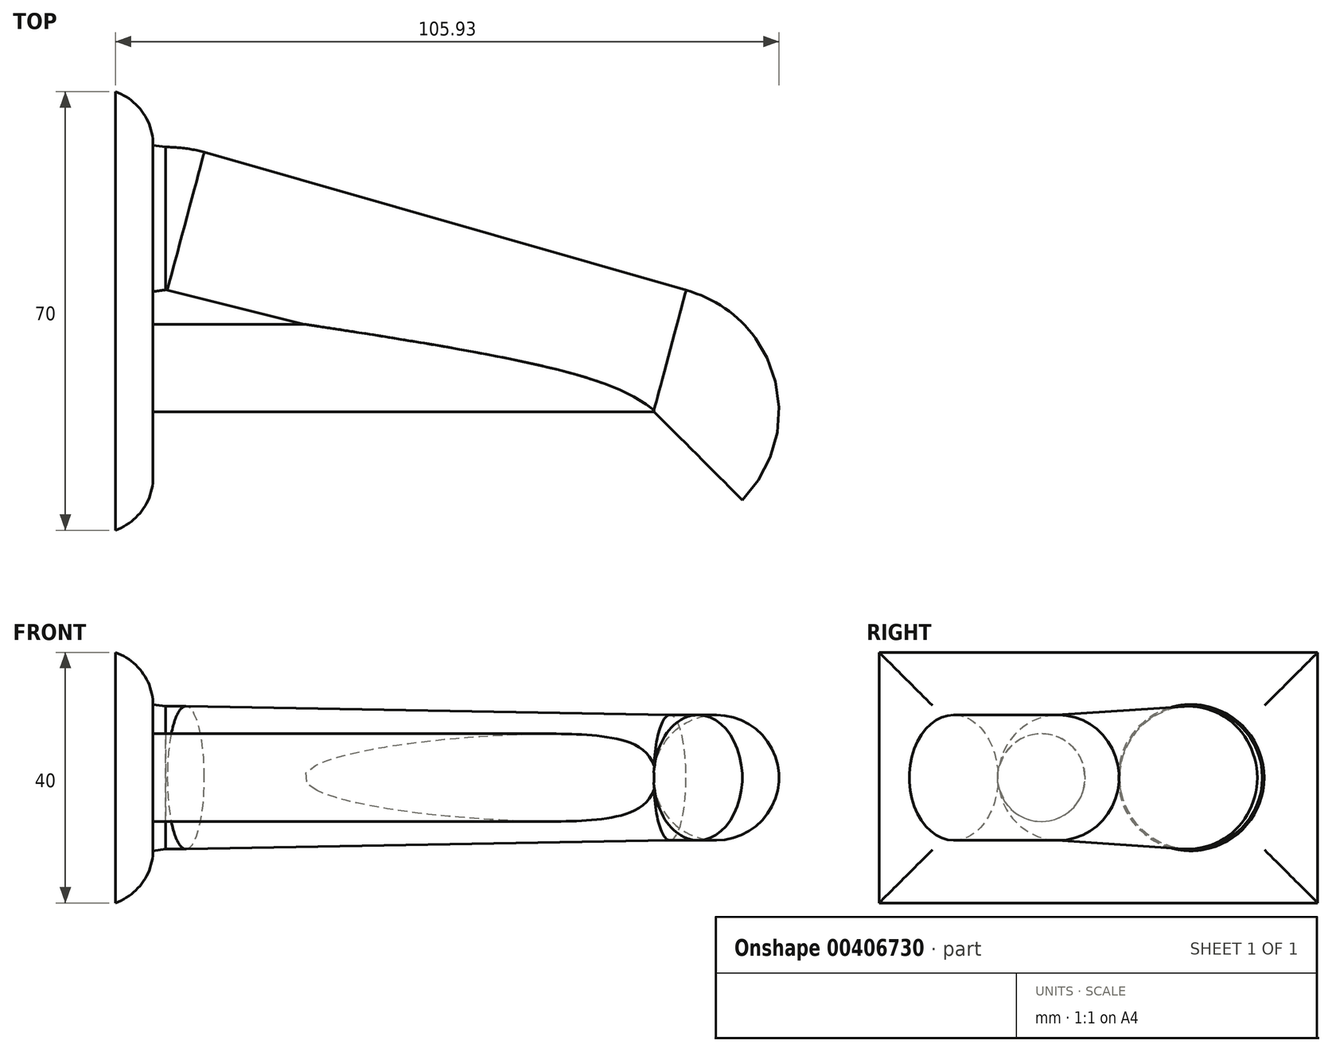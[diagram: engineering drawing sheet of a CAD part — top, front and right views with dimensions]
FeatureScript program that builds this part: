
annotation { "Feature Type Name" : "Feature", "Feature Type Description" : "" }
export const myFeature = defineFeature(function(context is Context, id is Id, definition is map)
    precondition{}
    {
        {
            var Q0;
            Q0=qCreatedBy(makeId("Front.planeOp"),FACE);
            var sketch = newSketch(context, id + "F0", { "sketchPlane" : qUnion([Q0])});
            skCircle(sketch, "E0", {"center": v(0, 0) * mm, "radius": 10 * mm});
            skSolve(sketch);
        }
        {
            var Q0;
            Q0=qCreatedBy(makeId("Front.planeOp"),FACE);
            var sketch = newSketch(context, id + "F1", { "sketchPlane" : qUnion([Q0])});
            skLineSegment(sketch, "E1", {"start": v(-10, 7.92) * mm, "end": v(-10, -9.36) * mm});
            skSolve(sketch);
        }
        {
            var Q0;
            Q0=makeQuery(id+"F0.imprint","IMPRINT",FACE,{"disambiguationData":[TD([[makeQuery(id+"F0.imprint","IMPRINT",EDGE,{"derivedFrom":sQuery(id+"F0.wireOp",EDGE,"E0")}),1.0]])]});
            var Q1;
            Q1=sQuery(id+"F1.wireOp",EDGE,"E1");
            revolve(context, id + "F2", {"entities" : qUnion([Q0]), "axis" : qUnion([Q1]), "revolveType" : RevolveType.TWO_DIRECTIONS, "angle" : 45 * degree, "angleBack" : 285 * degree});
        }
        {
            var Q0;
            Q0=makeQuery(id+"F2.opRevolve","CAP_FACE",FACE,{"disambiguationData":[OSD([sQuery(id+"F0.wireOp",EDGE,"E0")])],"isStart":true});
            extrude(context, id + "F3", {"entities" : qUnion([Q0]), "operationType" : NewBodyOperationType.ADD, "depth" : 80 * mm, "hasDraft" : true, "draftAngle" : 1 * degree});
        }
        {
            var Q0;
            Q0=makeQuery(id+"F3.opExtrude","CAP_FACE",FACE,{"disambiguationData":[OSD([sQuery(id+"F0.wireOp",EDGE,"E0")])],"isStart":false});
            var sketch = newSketch(context, id + "F4", { "sketchPlane" : qUnion([Q0])});
            skLineSegment(sketch, "E2", {"start": v(5.07, 0) * mm, "end": v(5.07, -9.96) * mm});
            skSolve(sketch);
        }
        {
            var Q0;
            Q0=makeQuery(id+"F4.imprint","IMPRINT",FACE,{"disambiguationData":[TD([[makeQuery(id+"F4.imprint","IMPRINT",EDGE,{"derivedFrom":makeQuery(id+"F3.opExtrude","CAP_EDGE",EDGE,{"disambiguationData":[OSD([sQuery(id+"F0.wireOp",EDGE,"E0")])],"isStart":false})}),-1.0]])]});
            var Q1;
            Q1=sQuery(id+"F4.wireOp",EDGE,"E2");
            revolve(context, id + "F5", {"operationType" : NewBodyOperationType.ADD, "entities" : qUnion([Q0]), "axis" : qUnion([Q1]), "revolveType" : RevolveType.ONE_DIRECTION, "oppositeDirection" : true, "angle" : 15 * degree});
        }
        {
            var Q0;
            Q0=makeQuery(id+"F5.opRevolve","CAP_FACE",FACE,{"disambiguationData":[OSD([sQuery(id+"F0.wireOp",EDGE,"E0")])],"isStart":false});
            extrude(context, id + "F6", {"entities" : qUnion([Q0]), "operationType" : NewBodyOperationType.ADD, "depth" : 5 * mm, "hasDraft" : true, "draftAngle" : 8 * degree});
        }
        {
            var Q0;
            Q0=makeQuery(id+"F6.opExtrude","CAP_FACE",FACE,{"disambiguationData":[OSD([sQuery(id+"F0.wireOp",EDGE,"E0")])],"isStart":false});
            var sketch = newSketch(context, id + "F7", { "sketchPlane" : qUnion([Q0])});
            skLineSegment(sketch, "E3.bottom", {"start": v(18.97, 20) * mm, "end": v(-51.03, 20) * mm});
            skLineSegment(sketch, "E3.top", {"start": v(18.97, -20) * mm, "end": v(-51.03, -20) * mm});
            skLineSegment(sketch, "E3.left", {"start": v(18.97, 20) * mm, "end": v(18.97, -20) * mm});
            skLineSegment(sketch, "E3.right", {"start": v(-51.03, 20) * mm, "end": v(-51.03, -20) * mm});
            skSolve(sketch);
        }
        {
            var Q0;
            Q0 = qSketchRegion(id + "F7", true);
            extrude(context, id + "F8", {"entities" : qUnion([Q0]), "operationType" : NewBodyOperationType.ADD, "depth" : 3 * mm, "hasSecondDirection" : true, "secondDirectionOppositeDirection" : true, "secondDirectionDepth" : 3 * mm});
        }
        {
            var Q0;
            Q0=makeQuery(id+"F8.opExtrude","CAP_FACE",FACE,{"disambiguationData":[OSD([sQuery(id+"F7.wireOp",EDGE,"E3.bottom"),sQuery(id+"F7.wireOp",EDGE,"E3.top"),sQuery(id+"F7.wireOp",EDGE,"E3.left"),sQuery(id+"F7.wireOp",EDGE,"E3.right")])],"isStart":true});
            var sketch = newSketch(context, id + "F9", { "sketchPlane" : qUnion([Q0])});
            skCircle(sketch, "E4", {"center": v(20.3, 0) * mm, "radius": 6.5 * mm});
            skSolve(sketch);
        }
        {
            var Q0;
            Q0=makeQuery(id+"F8.opExtrude","CAP_EDGE",EDGE,{"disambiguationData":[OSD([sQuery(id+"F7.wireOp",EDGE,"E3.top")])],"isStart":true});
            var Q1;
            Q1=makeQuery(id+"F8.opExtrude","CAP_EDGE",EDGE,{"disambiguationData":[OSD([sQuery(id+"F7.wireOp",EDGE,"E3.bottom")])],"isStart":true});
            var Q2;
            Q2=makeQuery(id+"F8.opExtrude","CAP_EDGE",EDGE,{"disambiguationData":[OSD([sQuery(id+"F7.wireOp",EDGE,"E3.left")])],"isStart":true});
            var Q3;
            Q3=makeQuery(id+"F8.opExtrude","CAP_EDGE",EDGE,{"disambiguationData":[OSD([sQuery(id+"F7.wireOp",EDGE,"E3.right")])],"isStart":true});
            fillet(context, id + "F10", {"entities" : qUnion([Q0, Q1, Q2, Q3]), "radius" : 9 * mm, "tangentPropagation" : true, "allowEdgeOverflow" : false});
        }
        {
            var Q0;
            Q0=makeQuery(id+"F9.imprint","IMPRINT",FACE,{"disambiguationData":[TD([[makeQuery(id+"F9.imprint","IMPRINT",EDGE,{"derivedFrom":sQuery(id+"F9.wireOp",EDGE,"E4")}),-1.0]])]});
            var sketch = newSketch(context, id + "F11", { "sketchPlane" : qUnion([Q0])});
            skLineSegment(sketch, "E5", {"start": v(28.42, -5.26) * mm, "end": v(28.42, 5.1) * mm});
            skSolve(sketch);
        }
        {
            var Q0;
            Q0=makeQuery(id+"F9.imprint","IMPRINT",FACE,{"disambiguationData":[TD([[makeQuery(id+"F9.imprint","IMPRINT",EDGE,{"derivedFrom":sQuery(id+"F9.wireOp",EDGE,"E4")}),1.0]])]});
            var Q1;
            Q1=sQuery(id+"F11.wireOp",EDGE,"E5");
            revolve(context, id + "F12", {"operationType" : NewBodyOperationType.ADD, "entities" : qUnion([Q0]), "axis" : qUnion([Q1]), "revolveType" : RevolveType.ONE_DIRECTION, "oppositeDirection" : true, "angle" : 20 * degree});
        }
        {
            var Q0;
            Q0=makeQuery(id+"F8.opExtrude","CAP_FACE",FACE,{"disambiguationData":[OSD([sQuery(id+"F7.wireOp",EDGE,"E3.bottom"),sQuery(id+"F7.wireOp",EDGE,"E3.top"),sQuery(id+"F7.wireOp",EDGE,"E3.left"),sQuery(id+"F7.wireOp",EDGE,"E3.right")])],"isStart":true});
            var sketch = newSketch(context, id + "F13", { "sketchPlane" : qUnion([Q0])});
            skCircle(sketch, "E6", {"center": v(6.92, 0) * mm, "radius": 7 * mm});
            skSolve(sketch);
        }
        {
            var Q0;
            Q0=makeQuery(id+"F13.imprint","IMPRINT",FACE,{"disambiguationData":[TD([[makeQuery(id+"F13.imprint","IMPRINT",EDGE,{"derivedFrom":sQuery(id+"F13.wireOp",EDGE,"E6")}),1.0]])]});
            extrude(context, id + "F14", {"entities" : qUnion([Q0]), "operationType" : NewBodyOperationType.ADD, "depth" : 85 * mm});
        }
    });
